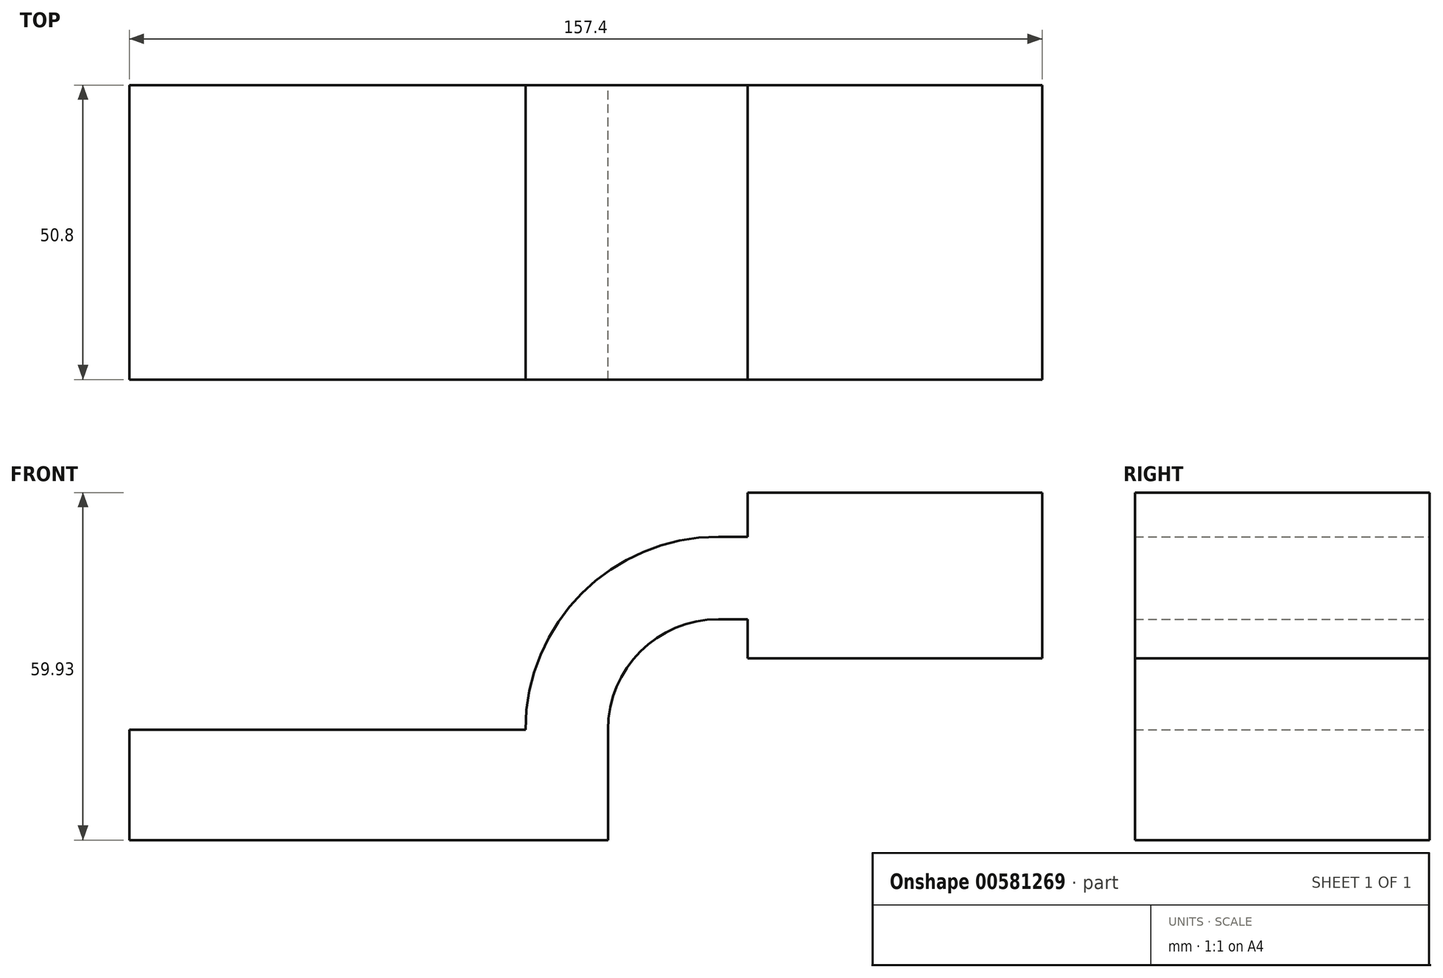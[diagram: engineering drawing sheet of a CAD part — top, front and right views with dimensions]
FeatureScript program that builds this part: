
annotation { "Feature Type Name" : "Feature", "Feature Type Description" : "" }
export const myFeature = defineFeature(function(context is Context, id is Id, definition is map)
    precondition{}
    {
        {
            var Q0;
            Q0=qCreatedBy(makeId("Front.planeOp"),FACE);
            var sketch = newSketch(context, id + "F0", { "sketchPlane" : qUnion([Q0])});
            skLineSegment(sketch, "E0.bottom", {"start": v(-41.28, 9.53) * mm, "end": v(41.27, 9.53) * mm});
            skLineSegment(sketch, "E0.top", {"start": v(-41.27, -9.53) * mm, "end": v(41.28, -9.53) * mm});
            skLineSegment(sketch, "E0.left", {"start": v(-41.28, 9.53) * mm, "end": v(-41.28, -9.52) * mm});
            skLineSegment(sketch, "E0.right", {"start": v(41.28, 9.53) * mm, "end": v(41.28, -9.52) * mm});
            skPoint(sketch, "E0.middle", {"position": v(0, 0) * mm});
            skPoint(sketch, "E1.middle", {"position": v(30.41, 32.88) * mm});
            skLineSegment(sketch, "E2.bottom", {"start": v(65.33, 50.4) * mm, "end": v(116.13, 50.4) * mm});
            skLineSegment(sketch, "E2.top", {"start": v(65.33, 21.83) * mm, "end": v(116.13, 21.83) * mm});
            skLineSegment(sketch, "E2.left", {"start": v(65.33, 50.4) * mm, "end": v(65.33, 21.83) * mm});
            skLineSegment(sketch, "E2.right", {"start": v(116.13, 50.4) * mm, "end": v(116.13, 21.83) * mm});
            skPoint(sketch, "E2.middle", {"position": v(90.73, 36.11) * mm});
            skArc(sketch, "E3", {"start": v(41.27, 9.53) * mm, "mid": v(46.85, 23) * mm, "end": v(60.32, 28.57) * mm});
            skLineSegment(sketch, "E4", {"start": v(60.32, 28.57) * mm, "end": v(80.76, 28.57) * mm});
            skLineSegment(sketch, "E5.0", {"start": v(60.32, 42.8) * mm, "end": v(80.76, 42.8) * mm});
            skArc(sketch, "E5.1", {"start": v(27.05, 9.53) * mm, "mid": v(36.8, 33.05) * mm, "end": v(60.32, 42.8) * mm});
            skFitSpline(sketch, "E6", {"points": [v(-41.28, 9.53) * mm, v(60.32, 42.8) * mm], "startDerivative": vector(84.6, 76.9) * mm, "endDerivative": vector(134.93, -31.9) * mm});
            skSolve(sketch);
        }
        {
            var Q0;
            {var subQ3=sQuery(id+"F0.wireOp",EDGE,"E2.bottom");Q0=makeQuery(id+"F0.imprint","IMPRINT",FACE,{"disambiguationData":[TD([[makeQuery(id+"F0.imprint","IMPRINT",EDGE,{"derivedFrom":subQ3}),-1.0]])]});}
            var Q1;
            {var subQ1=sQuery(id+"F0.wireOp",EDGE,"E3");Q1=makeQuery(id+"F0.imprint","IMPRINT",FACE,{"disambiguationData":[TD([[makeQuery(id+"F0.imprint","IMPRINT",EDGE,{"derivedFrom":subQ1}),1.0]])]});}
            var Q2;
            Q2=makeQuery(id+"F0.imprint","IMPRINT",FACE,{"disambiguationData":[TD([[makeQuery(id+"F0.imprint","IMPRINT",EDGE,{"derivedFrom":sQuery(id+"F0.wireOp",EDGE,"E0.top")}),1.0]])]});
            var Q3;
            {var subQ2=sQuery(id+"F0.wireOp",EDGE,"E5.1");Q3=makeQuery(id+"F0.imprint","IMPRINT",FACE,{"disambiguationData":[TD([[makeQuery(id+"F0.imprint","IMPRINT",EDGE,{"derivedFrom":subQ2}),1.0]])]});}
            extrude(context, id + "F1", {"entities" : qUnion([Q0, Q1, Q2, Q3]), "endBound" : BoundingType.SYMMETRIC, "depth" : 50.8 * mm, "offsetDistance" : 25.4 * mm});
        }
    });
